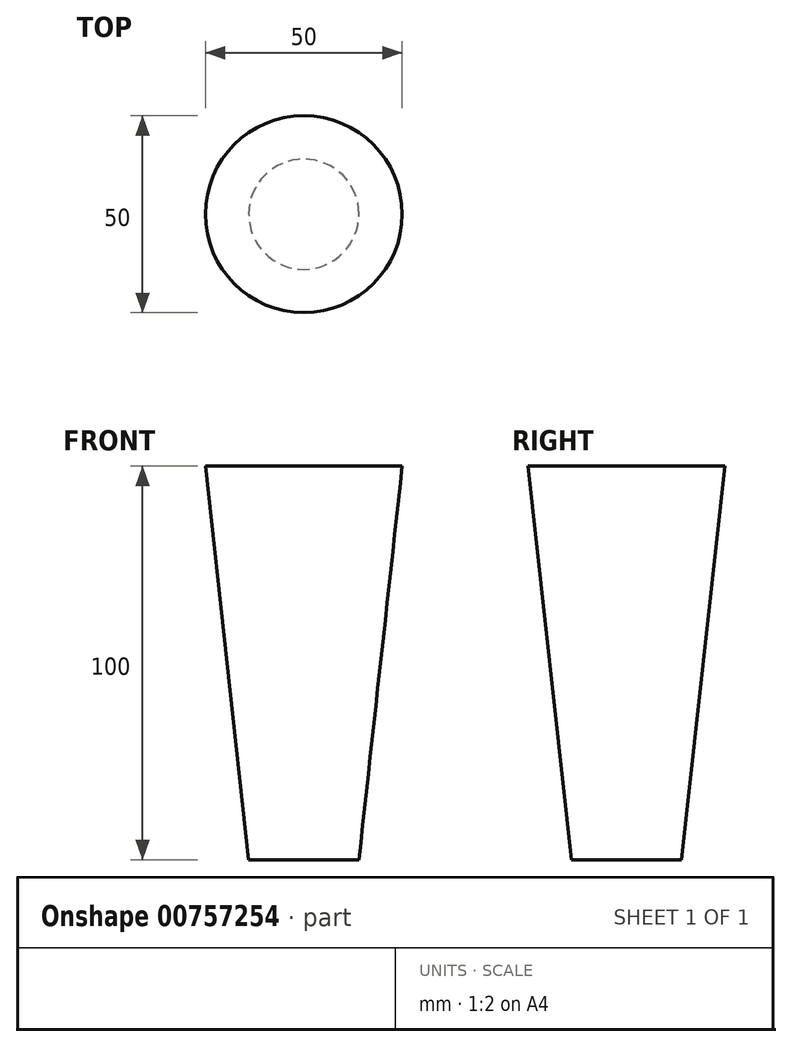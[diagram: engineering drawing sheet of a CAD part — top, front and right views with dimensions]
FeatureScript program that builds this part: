
annotation { "Feature Type Name" : "Feature", "Feature Type Description" : "" }
export const myFeature = defineFeature(function(context is Context, id is Id, definition is map)
    precondition{}
    {
        {
            var Q0;
            Q0=qCreatedBy(makeId("Top.planeOp"),FACE);
            var sketch = newSketch(context, id + "F0", { "sketchPlane" : qUnion([Q0])});
            skCircle(sketch, "E0", {"center": v(0, 0) * mm, "radius": 14 * mm});
            skSolve(sketch);
        }
        {
            var Q0;
            Q0=qCreatedBy(makeId("Top.planeOp"),FACE);
            cPlane(context, id + "F1", {"entities" : qUnion([Q0]), "cplaneType" : CPlaneType.OFFSET, "offset" : 100 * mm, "width" : 150 * mm, "height" : 150 * mm});
        }
        {
            var Q0;
            Q0=qCreatedBy(id+"F1.planeOp",FACE);
            var sketch = newSketch(context, id + "F2", { "sketchPlane" : qUnion([Q0])});
            skCircle(sketch, "E1", {"center": v(0, 0) * mm, "radius": 25 * mm});
            skSolve(sketch);
        }
        {
            var Q0;
            Q0=makeQuery(id+"F0.imprint","IMPRINT",FACE,{"disambiguationData":[TD([[makeQuery(id+"F0.imprint","IMPRINT",EDGE,{"derivedFrom":sQuery(id+"F0.wireOp",EDGE,"E0")}),1.0]])]});
            var Q1;
            Q1=makeQuery(id+"F2.imprint","IMPRINT",FACE,{"disambiguationData":[TD([[makeQuery(id+"F2.imprint","IMPRINT",EDGE,{"derivedFrom":sQuery(id+"F2.wireOp",EDGE,"E1")}),1.0]])]});
            loft(context, id + "F3", {"sheetProfilesArray" : [{ "sheetProfileEntities" : qUnion([Q0]) }, { "sheetProfileEntities" : qUnion([Q1]) }]});
        }
    });
